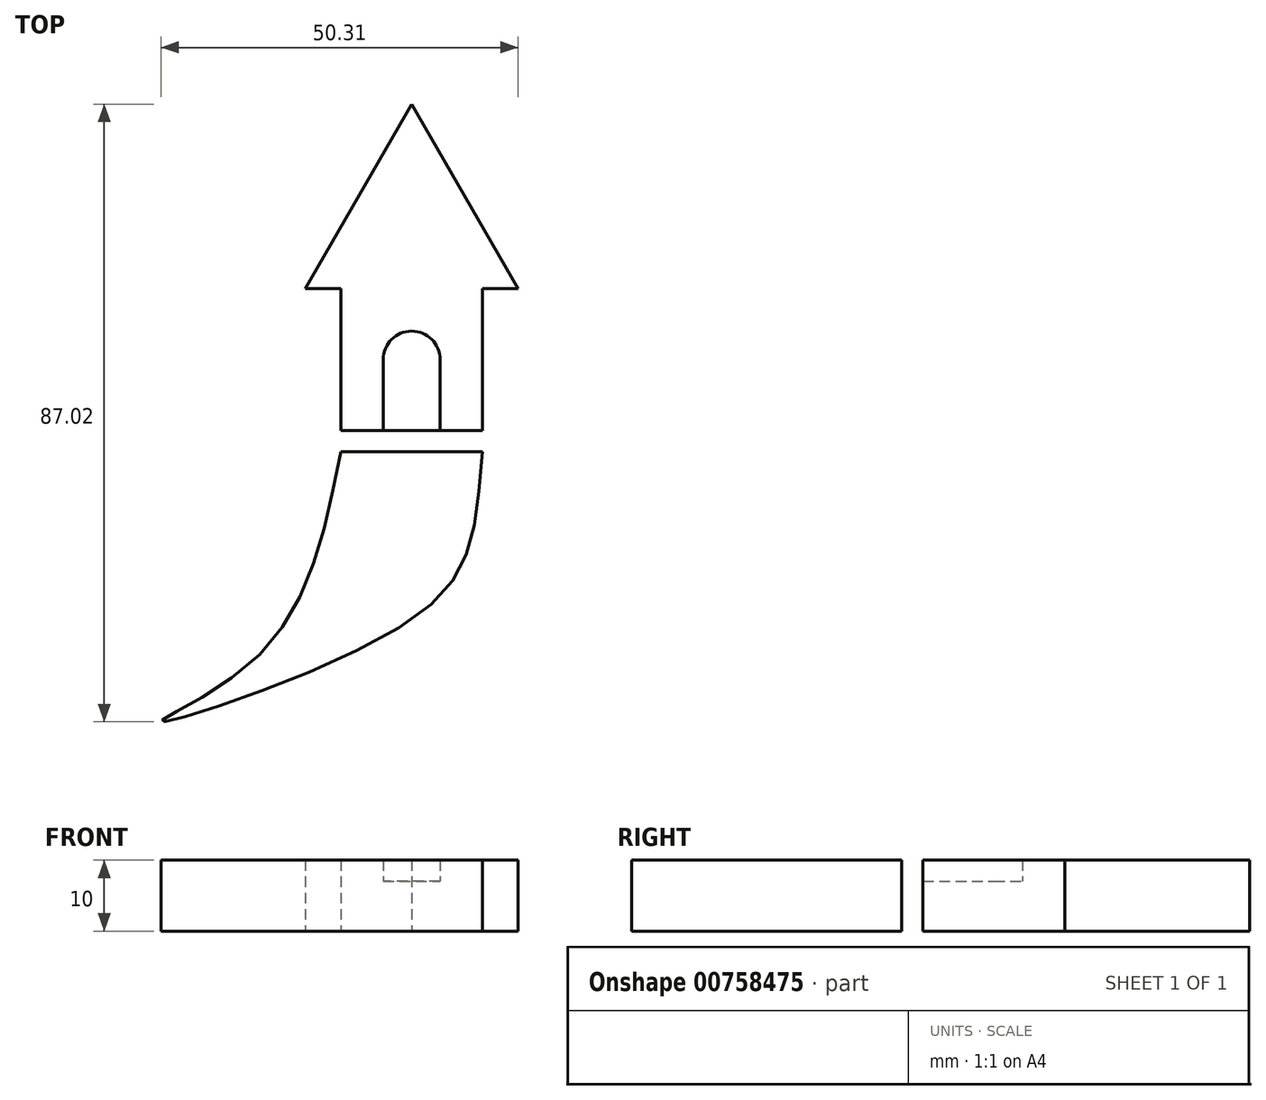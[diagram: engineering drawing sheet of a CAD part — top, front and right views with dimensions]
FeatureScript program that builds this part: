
annotation { "Feature Type Name" : "Feature", "Feature Type Description" : "" }
export const myFeature = defineFeature(function(context is Context, id is Id, definition is map)
    precondition{}
    {
        {
            var Q0;
            Q0=qCreatedBy(makeId("Top.planeOp"),FACE);
            var sketch = newSketch(context, id + "F0", { "sketchPlane" : qUnion([Q0])});
            skLineSegment(sketch, "E0.bottom", {"start": v(0, 0) * mm, "end": v(20, 0) * mm});
            skLineSegment(sketch, "E0.top", {"start": v(0, -20) * mm, "end": v(20, -20) * mm});
            skLineSegment(sketch, "E0.left", {"start": v(0, 0) * mm, "end": v(0, -20) * mm});
            skLineSegment(sketch, "E0.right", {"start": v(20, 0) * mm, "end": v(20, -20) * mm});
            skCircle(sketch, "E1.cCircle", {"center": v(10, 8.66) * mm, "radius": 8.66 * mm, "construction": true});
            skPoint(sketch, "E1.cCircle.perimeterSnap0", {"position": v(10, 0) * mm});
            skLineSegment(sketch, "E1.0", {"start": v(25, 0) * mm, "end": v(-5, 0) * mm});
            skLineSegment(sketch, "E1.1", {"start": v(-5, 0) * mm, "end": v(10, 25.98) * mm});
            skLineSegment(sketch, "E1.2", {"start": v(10, 25.98) * mm, "end": v(25, 0) * mm});
            skPoint(sketch, "E1.0.midPoint", {"position": v(10, 0) * mm});
            skPoint(sketch, "E1.0.midPoint.positionSnap0", {"position": v(10, 0) * mm});
            skLineSegment(sketch, "E2", {"start": v(6, -20) * mm, "end": v(6, -10) * mm});
            skLineSegment(sketch, "E3", {"start": v(6, -10) * mm, "end": v(14, -10) * mm});
            skLineSegment(sketch, "E4", {"start": v(14, -10) * mm, "end": v(14, -20) * mm});
            skArc(sketch, "E5", {"start": v(14, -10) * mm, "mid": v(10, -6) * mm, "end": v(6, -10) * mm});
            skLineSegment(sketch, "E6", {"start": v(0, -23) * mm, "end": v(20, -23) * mm});
            skFitSpline(sketch, "E7", {"points": [v(0, -23) * mm, v(-12.28, -52.38) * mm, v(-25.25, -61.03) * mm, v(10.4, -46.34) * mm, v(20, -23) * mm], "startDerivative": vector(-24.4, -128.25) * mm, "endDerivative": vector(13.05, 139.85) * mm});
            skSolve(sketch);
        }
        {
            var Q0;
            Q0=makeQuery(id+"F0.imprint","IMPRINT",FACE,{"disambiguationData":[TD([[makeQuery(id+"F0.imprint","IMPRINT",EDGE,{"derivedFrom":sQuery(id+"F0.wireOp",EDGE,"E6")}),-1.0]])]});
            var Q1;
            {var subQ0=sQuery(id+"F0.wireOp",EDGE,"E1.1");Q1=makeQuery(id+"F0.imprint","IMPRINT",FACE,{"disambiguationData":[TD([[makeQuery(id+"F0.imprint","IMPRINT",EDGE,{"derivedFrom":subQ0}),-1.0]])]});}
            var Q2;
            {var subQ1=sQuery(id+"F0.wireOp",EDGE,"E0.left");Q2=makeQuery(id+"F0.imprint","IMPRINT",FACE,{"disambiguationData":[TD([[makeQuery(id+"F0.imprint","IMPRINT",EDGE,{"derivedFrom":subQ1}),1.0]])]});}
            extrude(context, id + "F1", {"entities" : qUnion([Q0, Q1, Q2]), "depth" : 10 * mm, "offsetDistance" : 25 * mm});
        }
        {
            var Q0;
            {var subQ0=sQuery(id+"F0.wireOp",EDGE,"E2");Q0=makeQuery(id+"F0.imprint","IMPRINT",FACE,{"disambiguationData":[TD([[makeQuery(id+"F0.imprint","IMPRINT",EDGE,{"derivedFrom":subQ0}),-1.0]])]});}
            var Q1;
            Q1=makeQuery(id+"F0.imprint","IMPRINT",FACE,{"disambiguationData":[TD([[makeQuery(id+"F0.imprint","IMPRINT",EDGE,{"derivedFrom":sQuery(id+"F0.wireOp",EDGE,"E3")}),1.0]])]});
            extrude(context, id + "F2", {"entities" : qUnion([Q0, Q1]), "operationType" : NewBodyOperationType.ADD, "depth" : 7 * mm, "offsetDistance" : 25 * mm});
        }
    });
